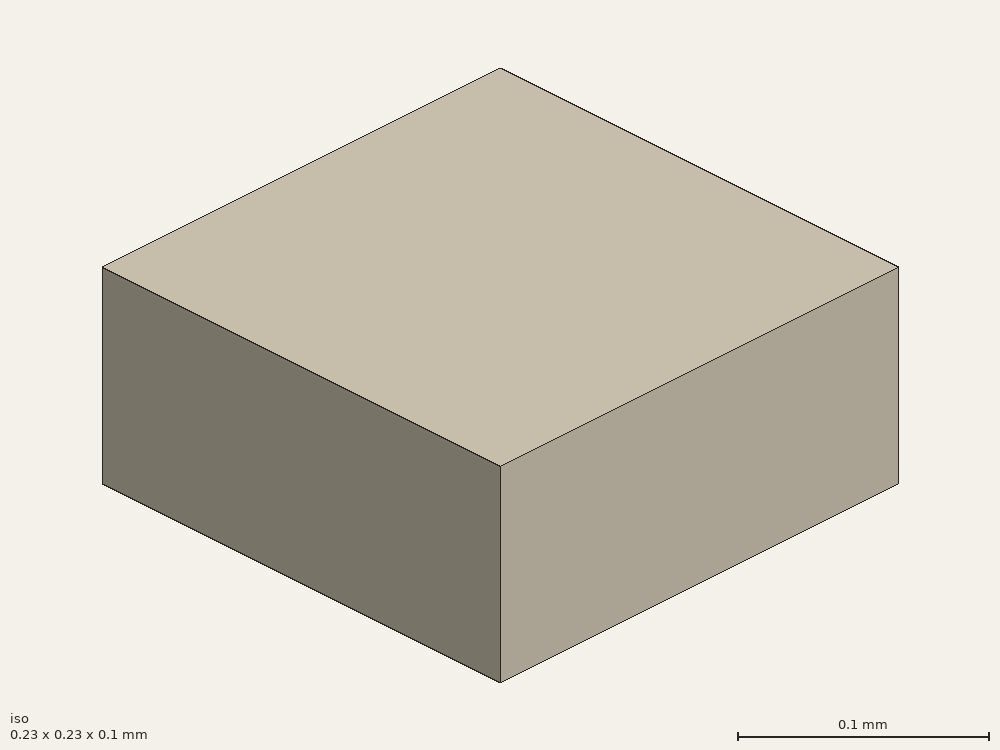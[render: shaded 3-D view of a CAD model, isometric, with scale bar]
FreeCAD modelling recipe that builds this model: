
FCSTD DOCUMENT  (FreeCAD 0.17R12607 (Git))
Label: 1616 RGB LED Red
License: CreativeCommons Attribution-ShareAlike
LicenseURL: http://creativecommons.org/licenses/by-sa/4.0/
objects: Sketcher::SketchObject×1, PartDesign::Pad×1, PartDesign::Body×1
note: 4 computed .brp shape members not serialized (recipe doc carries the construction recipe); baked Part::Feature solids carry a one-line shape summary decoded from their .brp

FEATURE [Sketcher::SketchObject] Sketch
  MapMode = 5
  Support = -> [XY_Plane]
  sketch-geometry (4):
    g0: LineSegment StartX=-0.1125 StartY=0.1125 StartZ=0 EndX=0.1125 EndY=0.1125 EndZ=0
    g1: LineSegment StartX=0.1125 StartY=0.1125 StartZ=0 EndX=0.1125 EndY=-0.1125 EndZ=0
    g2: LineSegment StartX=0.1125 StartY=-0.1125 StartZ=0 EndX=-0.1125 EndY=-0.1125 EndZ=0
    g3: LineSegment StartX=-0.1125 StartY=-0.1125 StartZ=0 EndX=-0.1125 EndY=0.1125 EndZ=0
  constraints (12):
    c: Coincident(g0,g1)
    c: Coincident(g1,g2)
    c: Coincident(g2,g3)
    c: Coincident(g3,g0)
    c: Horizontal(g0)
    c: Horizontal(g2)
    c: Vertical(g1)
    c: Vertical(g3)
    c: Symmetric(g0,g0,g-2)
    c: Symmetric(g0,g1,g-1)
    c: Equal(g0,g1)
    c: DistanceY(g1,g1) = 0.225
FEATURE [PartDesign::Pad] Pad
  Length = 0.1
  Length2 = 100
  Profile = -> Sketch
  Type = 0
FEATURE [PartDesign::Body] Body
  Group = -> [Sketch,Pad]
  Origin = -> Origin
  Tip = -> Pad
